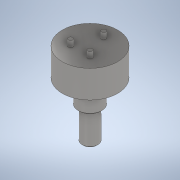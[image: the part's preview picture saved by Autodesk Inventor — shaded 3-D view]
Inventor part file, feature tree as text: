
AUTODESK INVENTOR PART (.ipt)
format: ipt  version: 2020 (Build 240168000, 168)  size: 168,960 bytes
history: native  units: in
note: dims shown in document units (in); Inventor stores cm internally (conversion verified against a paired STEP export)
features: sketch x4, extrude x3, revolve x1, chamfer x1
ambient origin geometry x8: Origin, YZ Plane, XZ Plane, XY Plane, X Axis, Y Axis, Z Axis, Center Point
bodies: Solid1 (feature_tree)
feature tree (9):
  revolve  "Revolution1"  [1 undecoded]
  chamfer  "Chamfer1"  Distance=0.203in
  extrude  "Extrusion1"  Depth=0.435in
  extrude  "Extrusion2"  Depth=0.4375in
  extrude  "Extrusion3"  Depth=0.098in
  sketch  "Sketch1"  dims[d0=0.875in d1=0.375in]
  sketch  "Sketch2"  dims[d2=0.059in]
  sketch  "Sketch3"  dims[d3=0.033in]
  sketch  "Sketch4"  dims[d4=0.1249in d5=0.203in d6=0.435in d7=0.4375in d8=0.1875in d9=90.0deg d10=0.0156in d11=0.125in d12=45.0deg d13=0.062in d14=0.29in d15=0.062in d16=0.0in d18=0.216in d19=0.375in d20=0.0in d21=0.435in d22=0.308in d23=0.07in d24=0.098in d25=0.0in]
note: 1 required parameter value undecoded (feature->parameter linkage not recoverable at this tier; creation-order binding heuristic only, values carry confidence <= 0.55)
